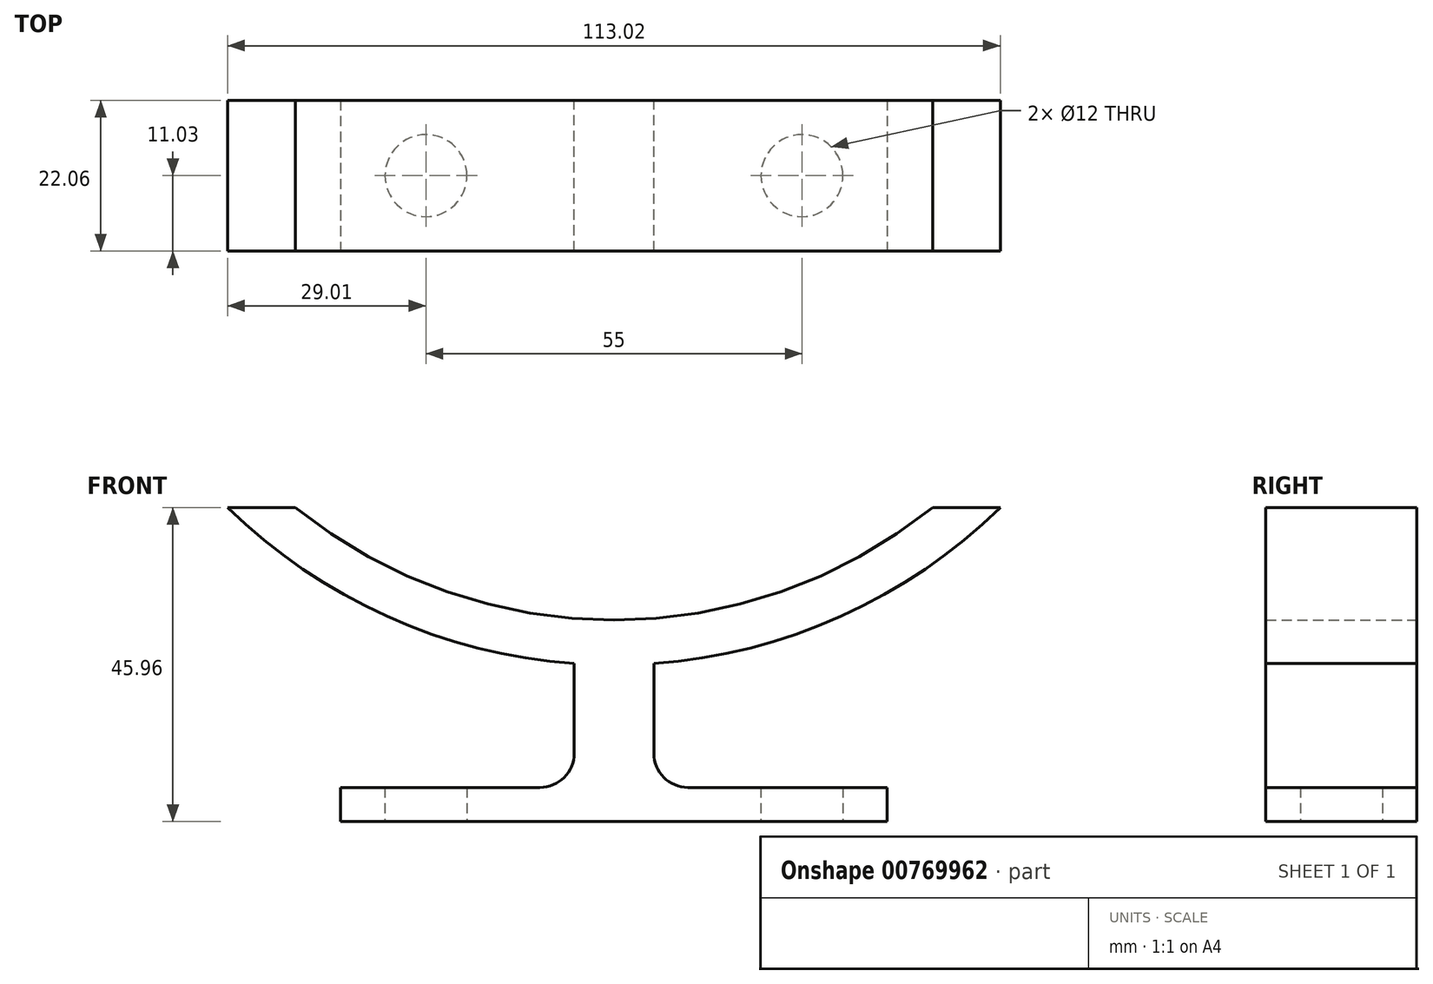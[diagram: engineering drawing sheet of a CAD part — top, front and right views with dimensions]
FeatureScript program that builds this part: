
annotation { "Feature Type Name" : "Feature", "Feature Type Description" : "" }
export const myFeature = defineFeature(function(context is Context, id is Id, definition is map)
    precondition{}
    {
        {
            var Q0;
            Q0=qCreatedBy(makeId("Top.planeOp"),FACE);
            var sketch = newSketch(context, id + "F0", { "sketchPlane" : qUnion([Q0])});
            skLineSegment(sketch, "E0.bottom", {"start": v(39.97, 11.03) * mm, "end": v(-39.97, 11.03) * mm});
            skLineSegment(sketch, "E0.top", {"start": v(39.97, -11.03) * mm, "end": v(-39.97, -11.03) * mm});
            skLineSegment(sketch, "E0.left", {"start": v(39.97, 11.03) * mm, "end": v(39.97, -11.03) * mm});
            skLineSegment(sketch, "E0.right", {"start": v(-39.97, 11.03) * mm, "end": v(-39.97, -11.03) * mm});
            skPoint(sketch, "E0.middle", {"position": v(0, 0) * mm});
            skLineSegment(sketch, "E1", {"start": v(-27.5, 0) * mm, "end": v(27.5, 0) * mm, "construction": true});
            skCircle(sketch, "E2", {"center": v(27.5, 0) * mm, "radius": 6 * mm});
            skCircle(sketch, "E3", {"center": v(-27.5, 0) * mm, "radius": 6 * mm});
            skSolve(sketch);
        }
        {
            var Q0;
            Q0 = qSketchRegion(id + "F0", true);
            extrude(context, id + "F1", {"entities" : qUnion([Q0]), "depth" : 5 * mm, "offsetDistance" : 25 * mm});
        }
        {
            var Q0;
            Q0=qCreatedBy(makeId("Front.planeOp"),FACE);
            var sketch = newSketch(context, id + "F2", { "sketchPlane" : qUnion([Q0])});
            skCircle(sketch, "E4", {"center": v(0, 103.69) * mm, "radius": 74.19 * mm});
            skCircle(sketch, "E5", {"center": v(0, 103.69) * mm, "radius": 80.79 * mm});
            skLineSegment(sketch, "E6", {"start": v(-75.96, 45.96) * mm, "end": v(79.25, 45.96) * mm});
            skLineSegment(sketch, "E7.bottom", {"start": v(5.82, 36.26) * mm, "end": v(-5.82, 36.26) * mm});
            skLineSegment(sketch, "E7.top", {"start": v(5.82, 0) * mm, "end": v(-5.82, 0) * mm});
            skLineSegment(sketch, "E7.left", {"start": v(5.82, 36.26) * mm, "end": v(5.82, 0) * mm});
            skLineSegment(sketch, "E7.right", {"start": v(-5.82, 36.26) * mm, "end": v(-5.82, 0) * mm});
            skPoint(sketch, "E7.middle", {"position": v(0, 18.13) * mm});
            skSolve(sketch);
        }
        {
            var Q0;
            {var subQ0=sQuery(id+"F2.wireOp",EDGE,"E7.right");var subQ1=sQuery(id+"F2.wireOp",EDGE,"E4");var subQ2=makeQuery(id+"F2.imprint","INTERSECT",VERTEX,{"derivedFrom":[subQ1,subQ0]});Q0=makeQuery(id+"F2.imprint","IMPRINT",FACE,{"disambiguationData":[TD([[makeQuery(id+"F2.imprint","IMPRINT",EDGE,{"disambiguationData":[TD([[subQ2,1.0]])],"derivedFrom":subQ1}),-1.0]])]});}
            var Q1;
            {var subQ0=sQuery(id+"F2.wireOp",EDGE,"E7.right");var subQ1=sQuery(id+"F2.wireOp",EDGE,"E4");var subQ2=makeQuery(id+"F2.imprint","INTERSECT",VERTEX,{"derivedFrom":[subQ1,subQ0]});Q1=makeQuery(id+"F2.imprint","IMPRINT",FACE,{"disambiguationData":[TD([[makeQuery(id+"F2.imprint","IMPRINT",EDGE,{"disambiguationData":[TD([[subQ2,-1.0]])],"derivedFrom":subQ1}),-1.0]])]});}
            var Q2;
            {var subQ0=sQuery(id+"F2.wireOp",EDGE,"E7.left");var subQ1=sQuery(id+"F2.wireOp",EDGE,"E4");var subQ2=makeQuery(id+"F2.imprint","INTERSECT",VERTEX,{"derivedFrom":[subQ1,subQ0]});Q2=makeQuery(id+"F2.imprint","IMPRINT",FACE,{"disambiguationData":[TD([[makeQuery(id+"F2.imprint","IMPRINT",EDGE,{"disambiguationData":[TD([[subQ2,-1.0]])],"derivedFrom":subQ1}),-1.0]])]});}
            var Q3;
            {var subQ5=sQuery(id+"F2.wireOp",EDGE,"E7.top");Q3=makeQuery(id+"F2.imprint","IMPRINT",FACE,{"disambiguationData":[TD([[makeQuery(id+"F2.imprint","IMPRINT",EDGE,{"derivedFrom":subQ5}),-1.0]])]});}
            var Q4;
            Q4=makeQuery(id+"F1.opExtrude","SWEPT_FACE",FACE,{"disambiguationData":[OSD([sQuery(id+"F0.wireOp",EDGE,"E0.top")])]});
            var Q5;
            Q5=makeQuery(id+"F1.opExtrude","SWEPT_FACE",FACE,{"disambiguationData":[OSD([sQuery(id+"F0.wireOp",EDGE,"E0.bottom")])]});
            extrude(context, id + "F3", {"entities" : qUnion([Q0, Q1, Q2, Q3]), "operationType" : NewBodyOperationType.ADD, "endBound" : BoundingType.UP_TO_SURFACE, "depth" : 25 * mm, "endBoundEntityFace" : qUnion([Q4]), "offsetDistance" : 25 * mm, "hasSecondDirection" : true, "secondDirectionBound" : SecondDirectionBoundingType.UP_TO_SURFACE, "secondDirectionOppositeDirection" : true, "secondDirectionDepth" : 25 * mm, "secondDirectionBoundEntityFace" : qUnion([Q5])});
        }
        {
            var Q0;
            {var subQ0=sQuery(id+"F2.wireOp",EDGE,"E7.right");var subQ1=sQuery(id+"F2.wireOp",EDGE,"E5");Q0=makeQuery(id+"F3.opExtrude","TWEAK_EDGE",EDGE,{"derivedFrom":[makeQuery(id+"F2.imprint","IMPRINT",EDGE,{"disambiguationData":[TD([[makeQuery(id+"F2.imprint","INTERSECT",VERTEX,{"disambiguationData":[OD(0.0)],"derivedFrom":[subQ1,sQuery(id+"F2.wireOp",EDGE,"E6")]}),-1.0]])],"derivedFrom":subQ1}),makeQuery(id+"F2.imprint","IMPRINT",EDGE,{"disambiguationData":[TD([[makeQuery(id+"F2.imprint","INTERSECT",VERTEX,{"derivedFrom":[sQuery(id+"F2.wireOp",EDGE,"E7.top"),subQ0]}),1.0]])],"derivedFrom":subQ0})]});}
            var Q1;
            {var subQ0=sQuery(id+"F2.wireOp",EDGE,"E7.left");var subQ1=sQuery(id+"F2.wireOp",EDGE,"E5");Q1=makeQuery(id+"F3.opExtrude","TWEAK_EDGE",EDGE,{"derivedFrom":[makeQuery(id+"F2.imprint","IMPRINT",EDGE,{"disambiguationData":[TD([[makeQuery(id+"F2.imprint","INTERSECT",VERTEX,{"disambiguationData":[OD(1.0)],"derivedFrom":[subQ1,sQuery(id+"F2.wireOp",EDGE,"E6")]}),1.0]])],"derivedFrom":subQ1}),makeQuery(id+"F2.imprint","IMPRINT",EDGE,{"disambiguationData":[TD([[makeQuery(id+"F2.imprint","INTERSECT",VERTEX,{"derivedFrom":[sQuery(id+"F2.wireOp",EDGE,"E7.top"),subQ0]}),1.0]])],"derivedFrom":subQ0})]});}
            var Q2;
            Q2=makeQuery(id+"F3.boolean.opBoolean","INTERSECT",EDGE,{"derivedFrom":[makeQuery(id+"F1.opExtrude","CAP_FACE",FACE,{"disambiguationData":[OSD([sQuery(id+"F0.wireOp",EDGE,"E0.bottom"),sQuery(id+"F0.wireOp",EDGE,"E0.top"),sQuery(id+"F0.wireOp",EDGE,"E0.left"),sQuery(id+"F0.wireOp",EDGE,"E0.right"),sQuery(id+"F0.wireOp",EDGE,"E2"),sQuery(id+"F0.wireOp",EDGE,"E3")])],"isStart":false}),makeQuery(id+"F3.opExtrude","SWEPT_FACE",FACE,{"disambiguationData":[OSD([sQuery(id+"F2.wireOp",EDGE,"E7.left")])]})]});
            var Q3;
            Q3=makeQuery(id+"F3.boolean.opBoolean","INTERSECT",EDGE,{"derivedFrom":[makeQuery(id+"F1.opExtrude","CAP_FACE",FACE,{"disambiguationData":[OSD([sQuery(id+"F0.wireOp",EDGE,"E0.bottom"),sQuery(id+"F0.wireOp",EDGE,"E0.top"),sQuery(id+"F0.wireOp",EDGE,"E0.left"),sQuery(id+"F0.wireOp",EDGE,"E0.right"),sQuery(id+"F0.wireOp",EDGE,"E2"),sQuery(id+"F0.wireOp",EDGE,"E3")])],"isStart":false}),makeQuery(id+"F3.opExtrude","SWEPT_FACE",FACE,{"disambiguationData":[OSD([sQuery(id+"F2.wireOp",EDGE,"E7.right")])]})]});
            var Q4;
            {var subQ0=sQuery(id+"F2.wireOp",EDGE,"E6");var subQ1=sQuery(id+"F2.wireOp",EDGE,"E5");var subQ2=makeQuery(id+"F2.imprint","INTERSECT",VERTEX,{"disambiguationData":[OD(0.0)],"derivedFrom":[subQ1,subQ0]});Q4=makeQuery(id+"F3.opExtrude","TWEAK_EDGE",EDGE,{"derivedFrom":[makeQuery(id+"F2.imprint","IMPRINT",EDGE,{"disambiguationData":[TD([[subQ2,-1.0]])],"derivedFrom":subQ1}),makeQuery(id+"F2.imprint","IMPRINT",EDGE,{"disambiguationData":[TD([[subQ2,-1.0]])],"derivedFrom":subQ0})]});}
            var Q5;
            {var subQ0=sQuery(id+"F2.wireOp",EDGE,"E6");var subQ1=sQuery(id+"F2.wireOp",EDGE,"E5");var subQ2=makeQuery(id+"F2.imprint","INTERSECT",VERTEX,{"disambiguationData":[OD(1.0)],"derivedFrom":[subQ1,subQ0]});Q5=makeQuery(id+"F3.opExtrude","TWEAK_EDGE",EDGE,{"derivedFrom":[makeQuery(id+"F2.imprint","IMPRINT",EDGE,{"disambiguationData":[TD([[subQ2,1.0]])],"derivedFrom":subQ1}),makeQuery(id+"F2.imprint","IMPRINT",EDGE,{"disambiguationData":[TD([[subQ2,1.0]])],"derivedFrom":subQ0})]});}
            fillet(context, id + "F4", {"entities" : qUnion([Q0, Q1, Q2, Q3, Q4, Q5]), "radius" : 5 * mm, "tangentPropagation" : true, "allowEdgeOverflow" : false});
        }
    });
